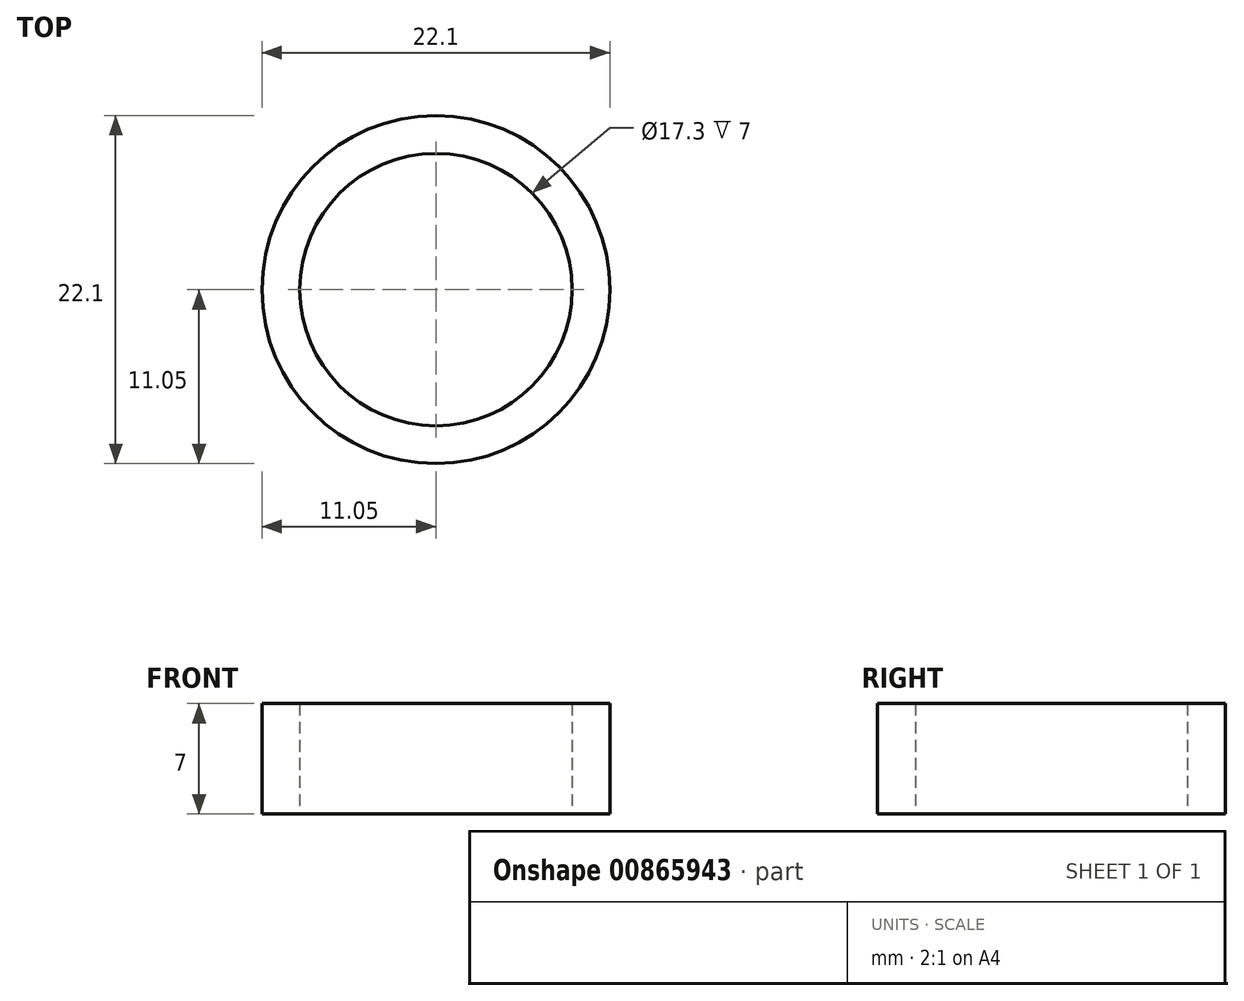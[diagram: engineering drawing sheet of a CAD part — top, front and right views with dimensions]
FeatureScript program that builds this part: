
annotation { "Feature Type Name" : "Feature", "Feature Type Description" : "" }
export const myFeature = defineFeature(function(context is Context, id is Id, definition is map)
    precondition{}
    {
        {
            var Q0;
            Q0=qCreatedBy(makeId("Top.planeOp"),FACE);
            var sketch = newSketch(context, id + "F0", { "sketchPlane" : qUnion([Q0])});
            skCircle(sketch, "E0", {"center": v(0, 0) * mm, "radius": 11.05 * mm});
            skCircle(sketch, "E1", {"center": v(0, 0) * mm, "radius": 8.65 * mm});
            skSolve(sketch);
        }
        {
            var Q0;
            Q0 = qSketchRegion(id + "F0", true);
            extrude(context, id + "F1", {"entities" : qUnion([Q0]), "depth" : 7 * mm, "offsetDistance" : 25 * mm});
        }
    });
